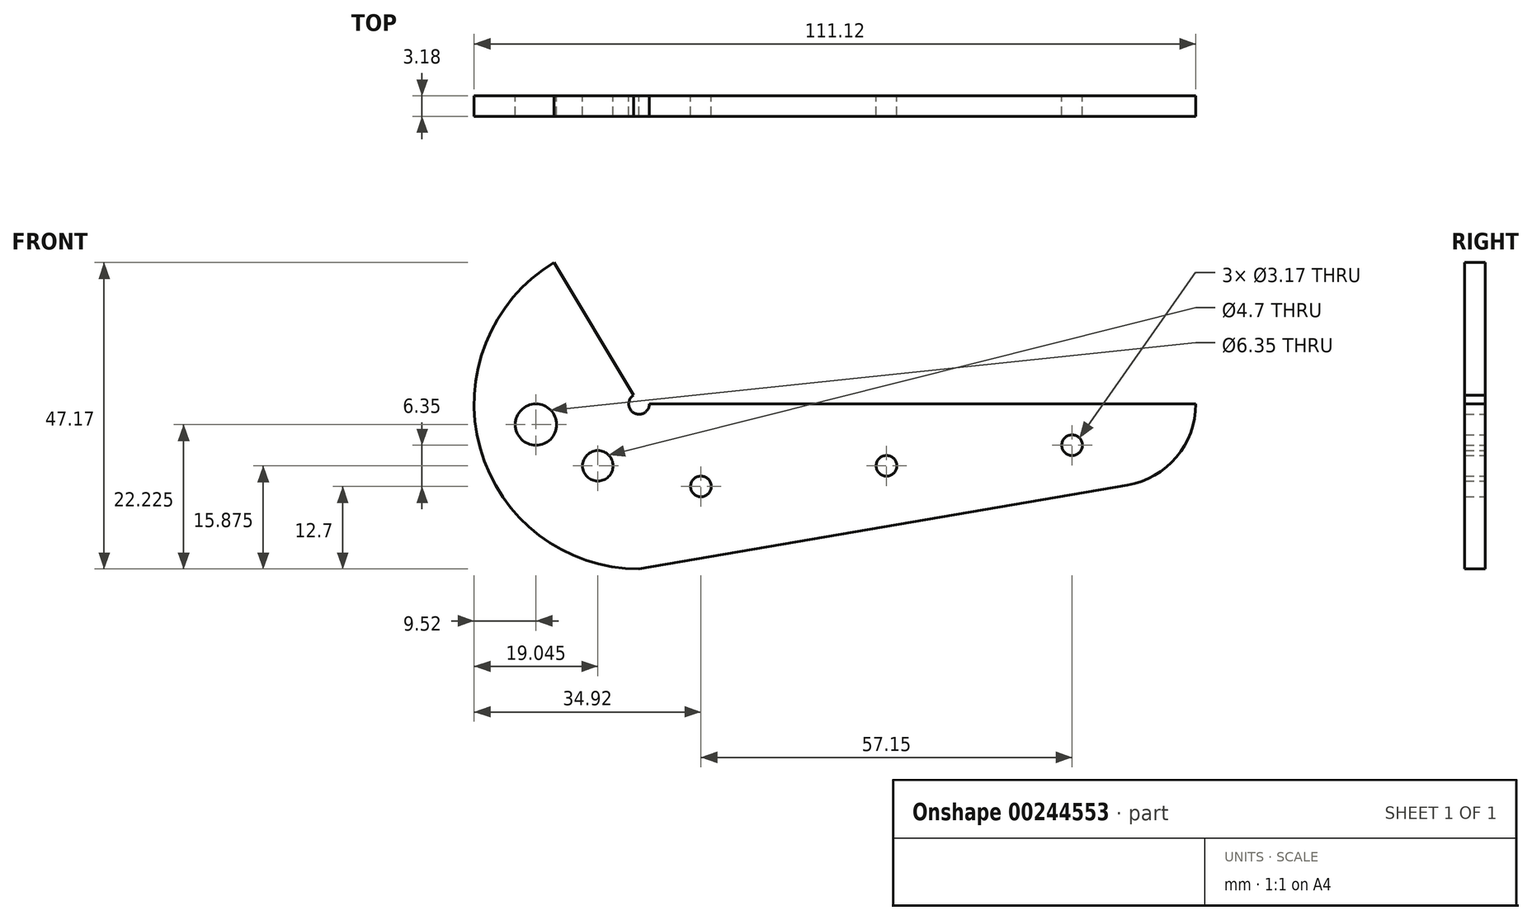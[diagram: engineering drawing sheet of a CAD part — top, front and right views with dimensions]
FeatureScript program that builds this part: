
annotation { "Feature Type Name" : "Feature", "Feature Type Description" : "" }
export const myFeature = defineFeature(function(context is Context, id is Id, definition is map)
    precondition{}
    {
        {
            var Q0;
            Q0=qCreatedBy(makeId("Front.planeOp"),FACE);
            var sketch = newSketch(context, id + "F0", { "sketchPlane" : qUnion([Q0])});
            skLineSegment(sketch, "E0", {"start": v(0, 0) * mm, "end": v(0, 25.4) * mm});
            skArc(sketch, "E1", {"start": v(-10.55, -12.52) * mm, "mid": v(-3, -8.19) * mm, "end": v(0, 0) * mm});
            skArc(sketch, "E2", {"start": v(-98.8, 21.77) * mm, "mid": v(-110.2, -6.79) * mm, "end": v(-85.72, -25.4) * mm});
            skLineSegment(sketch, "E3", {"start": v(-85.72, -25.4) * mm, "end": v(-10.55, -12.52) * mm});
            skPoint(sketch, "E4.orphan", {"position": v(0, -25.4) * mm});
            skLineSegment(sketch, "E5", {"start": v(0, 0) * mm, "end": v(-84.14, 0) * mm});
            skLineSegment(sketch, "E6", {"start": v(-98.8, 21.77) * mm, "end": v(-86.54, 1.36) * mm});
            skArc(sketch, "E7", {"start": v(-86.54, 1.36) * mm, "mid": v(-86.5, -1.38) * mm, "end": v(-84.14, 0) * mm});
            skCircle(sketch, "E8", {"center": v(-92.08, -9.53) * mm, "radius": 2.35 * mm});
            skCircle(sketch, "E9", {"center": v(-101.6, -3.18) * mm, "radius": 3.18 * mm});
            skCircle(sketch, "E10", {"center": v(-76.2, -12.7) * mm, "radius": 1.59 * mm});
            skCircle(sketch, "E11", {"center": v(-47.63, -9.53) * mm, "radius": 1.59 * mm});
            skCircle(sketch, "E12", {"center": v(-19.05, -6.35) * mm, "radius": 1.59 * mm});
            skSolve(sketch);
        }
        {
            var Q0;
            Q0=makeQuery(id+"F0.imprint","IMPRINT",FACE,{"disambiguationData":[TD([[makeQuery(id+"F0.imprint","IMPRINT",EDGE,{"derivedFrom":sQuery(id+"F0.wireOp",EDGE,"E1")}),1.0]])]});
            extrude(context, id + "F1", {"entities" : qUnion([Q0]), "depth" : 3.17 * mm});
        }
    });
